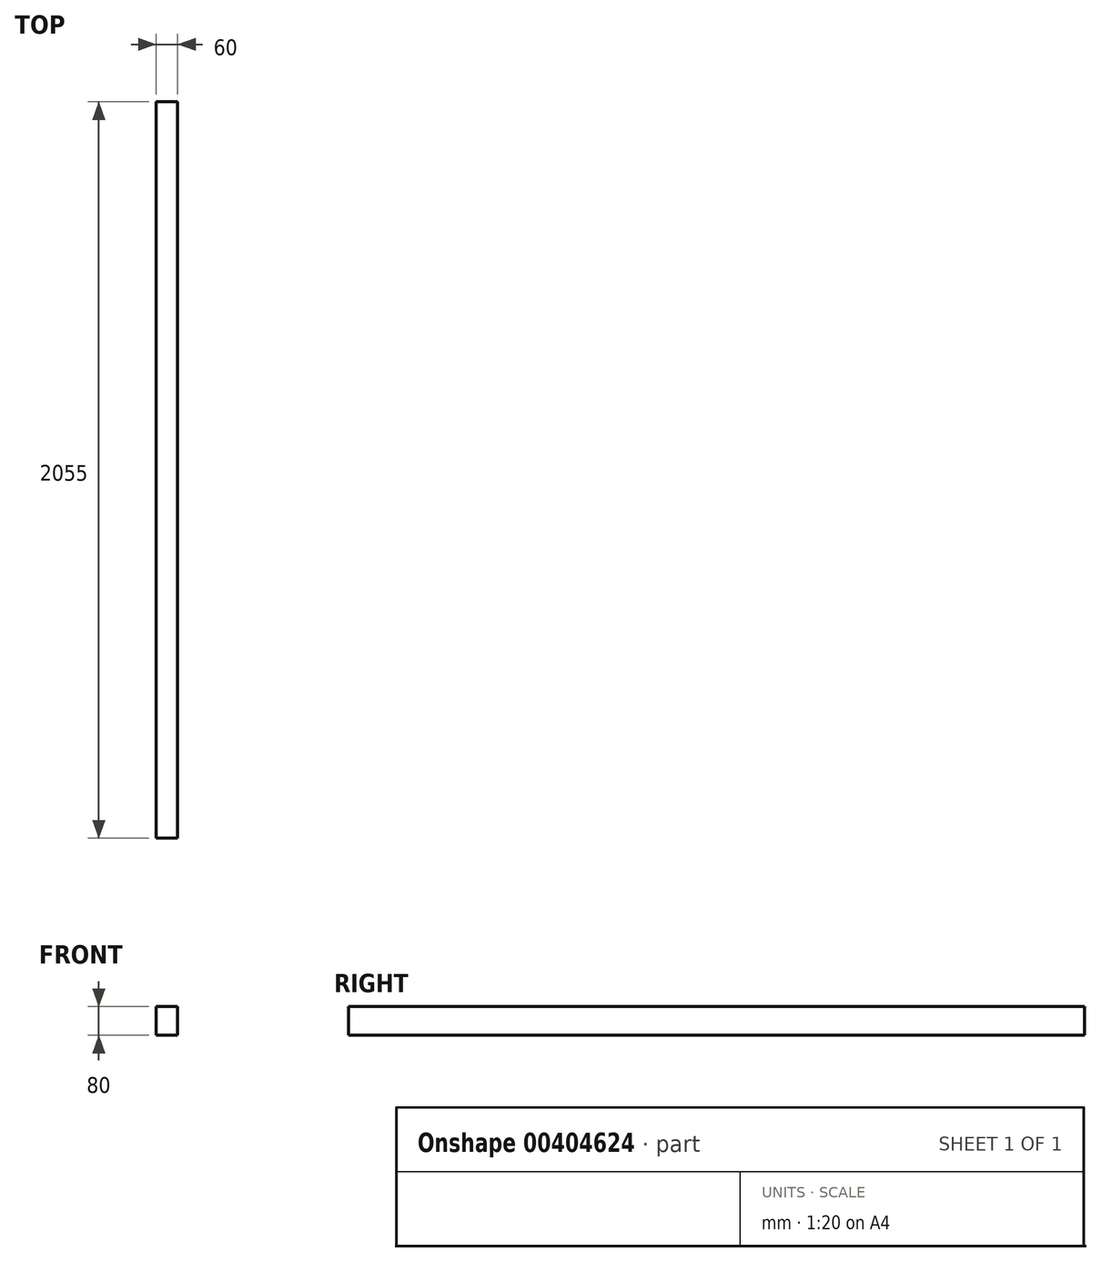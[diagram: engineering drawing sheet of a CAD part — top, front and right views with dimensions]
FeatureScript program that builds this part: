
annotation { "Feature Type Name" : "Feature", "Feature Type Description" : "" }
export const myFeature = defineFeature(function(context is Context, id is Id, definition is map)
    precondition{}
    {
        {
            var Q0;
            Q0=qCreatedBy(makeId("Front.planeOp"),FACE);
            var sketch = newSketch(context, id + "F0", { "sketchPlane" : qUnion([Q0])});
            skLineSegment(sketch, "E0.bottom", {"start": v(-30, 40) * mm, "end": v(30, 40) * mm});
            skLineSegment(sketch, "E0.top", {"start": v(-30, -40) * mm, "end": v(30, -40) * mm});
            skLineSegment(sketch, "E0.left", {"start": v(-30, 40) * mm, "end": v(-30, -40) * mm});
            skLineSegment(sketch, "E0.right", {"start": v(30, 40) * mm, "end": v(30, -40) * mm});
            skSolve(sketch);
        }
        {
            var Q0;
            Q0=qSketchRegion(id+"F0",true);
            extrude(context, id + "F1", {"entities" : qUnion([Q0]), "depth" : (3155 - 1100) * mm});
        }
    });
